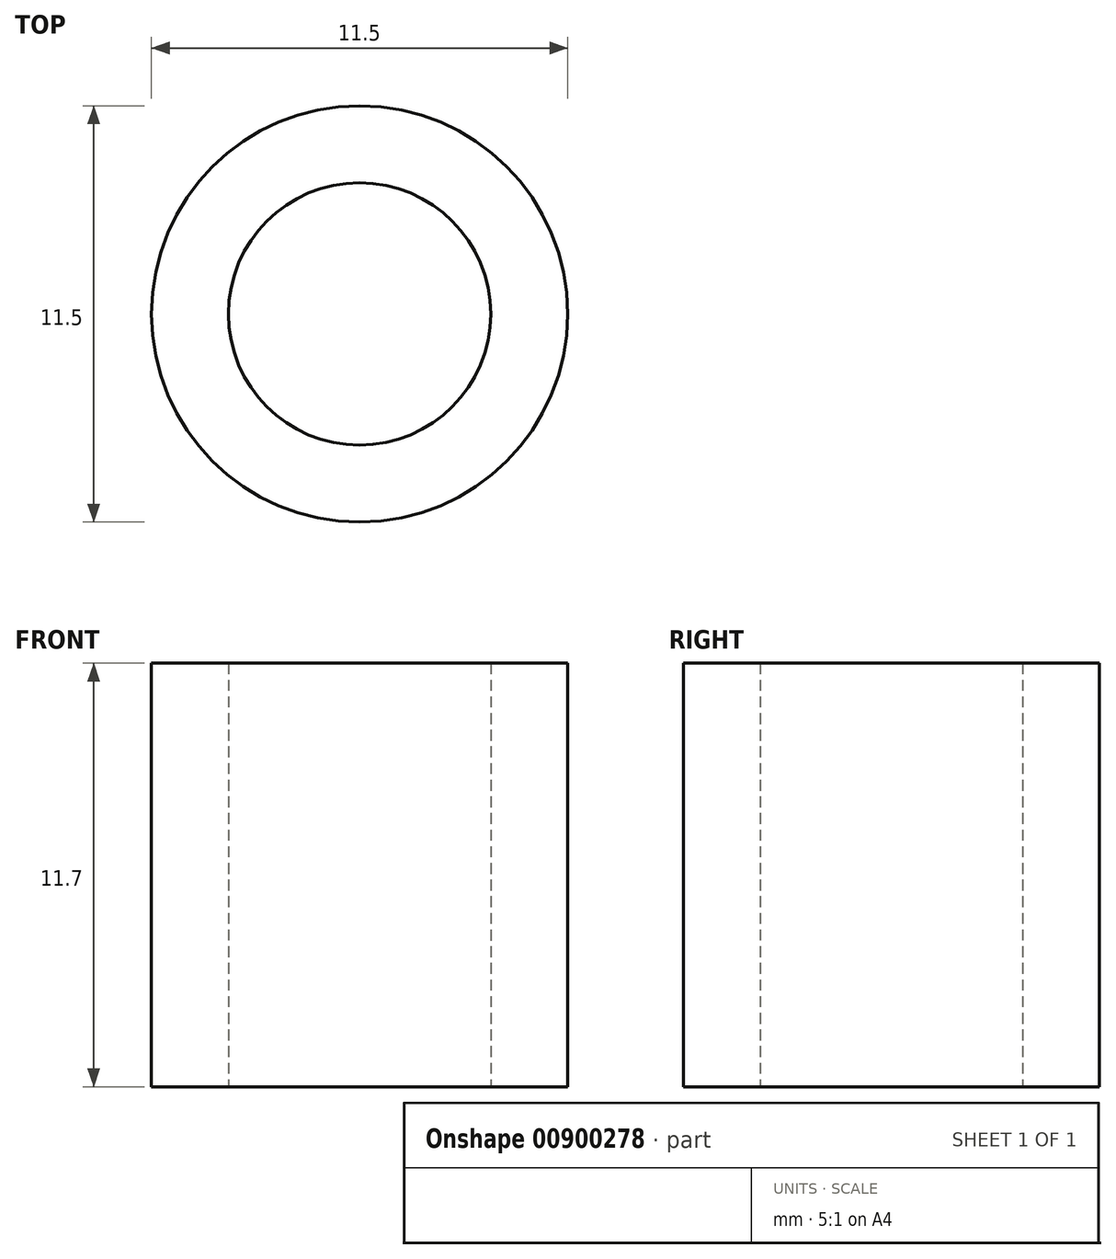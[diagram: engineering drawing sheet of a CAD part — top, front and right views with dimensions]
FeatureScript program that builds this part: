
annotation { "Feature Type Name" : "Feature", "Feature Type Description" : "" }
export const myFeature = defineFeature(function(context is Context, id is Id, definition is map)
    precondition{}
    {
        {
            var Q0;
            Q0=qCreatedBy(makeId("Top.planeOp"),FACE);
            var sketch = newSketch(context, id + "F0", { "sketchPlane" : qUnion([Q0])});
            skCircle(sketch, "E0", {"center": v(0, 0) * mm, "radius": 3.62 * mm});
            skCircle(sketch, "E1", {"center": v(0, 0) * mm, "radius": 5.75 * mm});
            skSolve(sketch);
        }
        {
            var Q0;
            Q0=makeQuery(id+"F0.imprint","IMPRINT",FACE,{"disambiguationData":[TD([[makeQuery(id+"F0.imprint","IMPRINT",EDGE,{"derivedFrom":sQuery(id+"F0.wireOp",EDGE,"E0")}),-1.0]])]});
            extrude(context, id + "F1", {"entities" : qUnion([Q0]), "depth" : 11.7 * mm, "offsetDistance" : 25.4 * mm});
        }
    });
